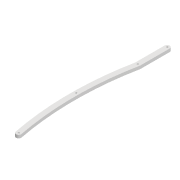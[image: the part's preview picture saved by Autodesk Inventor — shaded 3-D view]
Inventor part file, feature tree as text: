
AUTODESK INVENTOR PART (.ipt)
format: ipt  version: 2022 (Build 260153000, 153)  size: 103,936 bytes
history: native  units: mm
features: extrude x1
ambient origin geometry x8: Origin, YZ Plane, XZ Plane, XY Plane, X Axis, Y Axis, Z Axis, Center Point
bodies: Solid1 (feature_tree)
feature tree (1):
  extrude  "Extrusion1"  Depth=3.3mm
